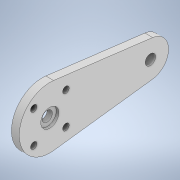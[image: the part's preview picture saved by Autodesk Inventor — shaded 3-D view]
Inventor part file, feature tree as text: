
AUTODESK INVENTOR PART (.ipt)
format: ipt  version: 2020 (Build 240168000, 168)  size: 160,256 bytes
history: native  units: mm
features: extrude x3, sketch x3, projected_geometry x1
ambient origin geometry x8: Origin, YZ Plane, XZ Plane, XY Plane, X Axis, Y Axis, Z Axis, Center Point
bodies: Body1 (feature_tree)
feature tree (7):
  extrude  "Выдавливание4"  Depth=18.6mm
  extrude  "Выдавливание5"  Depth=12.2mm
  extrude  "Выдавливание6"  Depth=9.7mm
  sketch  "Эскиз1"
  sketch  "Эскиз4"
  projected_geometry  "Спроецированная петля3"
  sketch  "Эскиз5"
